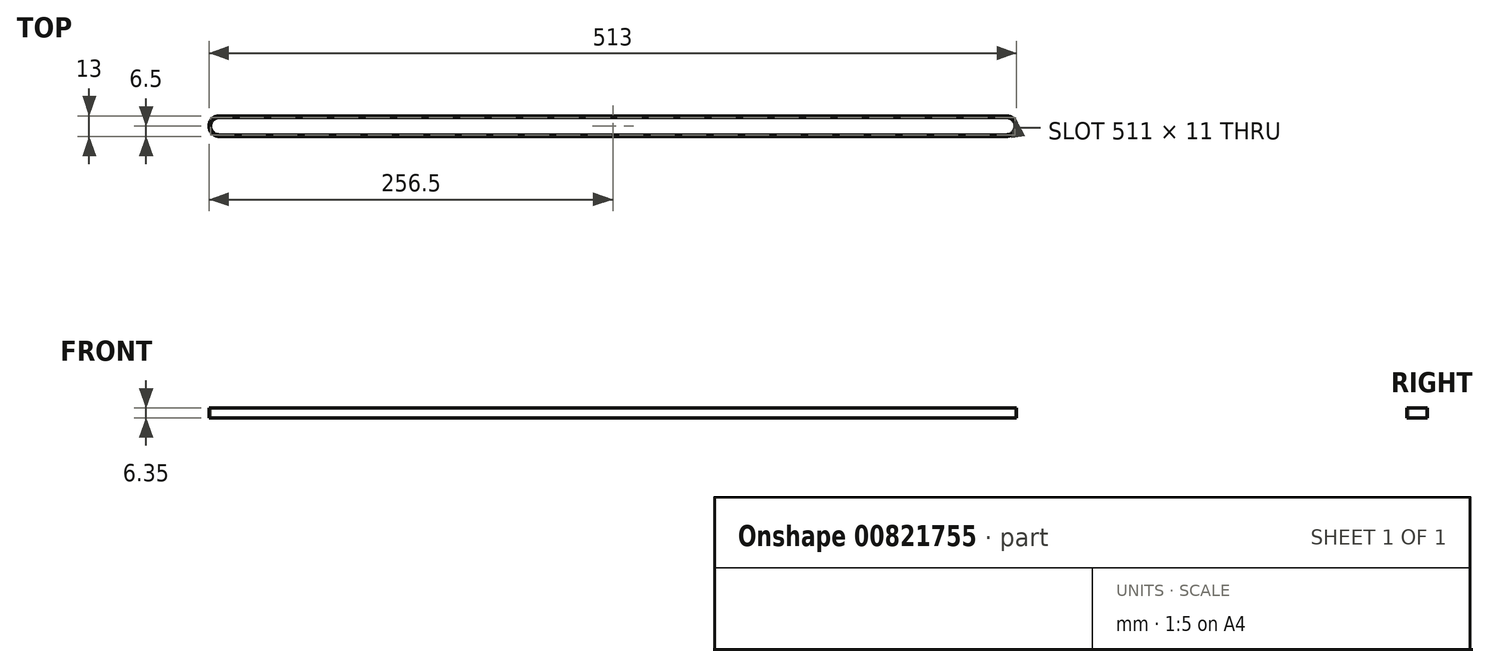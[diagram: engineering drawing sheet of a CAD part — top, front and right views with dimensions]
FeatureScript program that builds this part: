
annotation { "Feature Type Name" : "Feature", "Feature Type Description" : "" }
export const myFeature = defineFeature(function(context is Context, id is Id, definition is map)
    precondition{}
    {
        {
            var Q0;
            Q0=qCreatedBy(makeId("Top.planeOp"),FACE);
            var sketch = newSketch(context, id + "F0", { "sketchPlane" : qUnion([Q0])});
            skLineSegment(sketch, "E0.bottom", {"start": v(-250, 6.5) * mm, "end": v(250, 6.5) * mm});
            skLineSegment(sketch, "E0.top", {"start": v(-250, -6.5) * mm, "end": v(250, -6.5) * mm});
            skPoint(sketch, "E0.middle", {"position": v(0, 0) * mm});
            skArc(sketch, "E1", {"start": v(-250, 6.5) * mm, "mid": v(-256.5, 0) * mm, "end": v(-250, -6.5) * mm});
            skArc(sketch, "E2", {"start": v(250, -6.5) * mm, "mid": v(256.5, 0) * mm, "end": v(250, 6.5) * mm});
            skArc(sketch, "E3.0", {"start": v(250, -5.5) * mm, "mid": v(255.5, 0) * mm, "end": v(250, 5.5) * mm});
            skLineSegment(sketch, "E3.1", {"start": v(-250, -5.5) * mm, "end": v(250, -5.5) * mm});
            skArc(sketch, "E3.2", {"start": v(-250, 5.5) * mm, "mid": v(-255.5, 0) * mm, "end": v(-250, -5.5) * mm});
            skLineSegment(sketch, "E3.3", {"start": v(-250, 5.5) * mm, "end": v(250, 5.5) * mm});
            skSolve(sketch);
        }
        {
            var Q0;
            Q0 = qSketchRegion(id + "F0", true);
            extrude(context, id + "F1", {"entities" : qUnion([Q0]), "depth" : 6.35 * mm, "offsetDistance" : 25 * mm});
        }
    });
